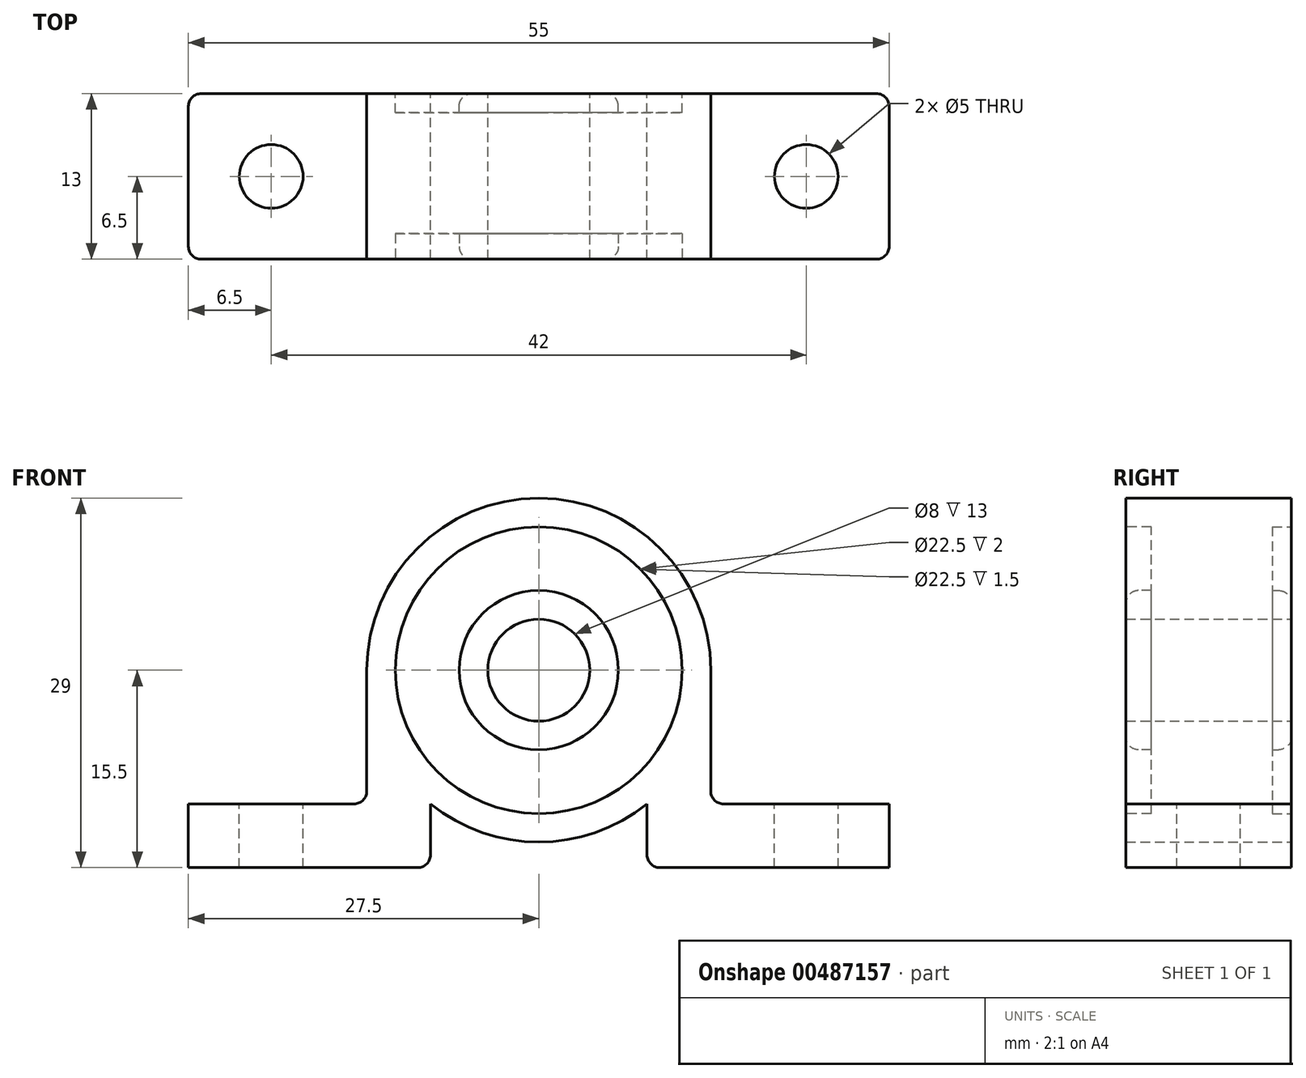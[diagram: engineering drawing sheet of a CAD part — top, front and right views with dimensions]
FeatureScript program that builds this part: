
annotation { "Feature Type Name" : "Feature", "Feature Type Description" : "" }
export const myFeature = defineFeature(function(context is Context, id is Id, definition is map)
    precondition{}
    {
        {
            var Q0;
            Q0=qCreatedBy(makeId("Front.planeOp"),FACE);
            var sketch = newSketch(context, id + "F0", { "sketchPlane" : qUnion([Q0])});
            skLineSegment(sketch, "E0.bottom", {"start": v(-27.5, 0) * mm, "end": v(-8.5, 0) * mm});
            skLineSegment(sketch, "E0.top", {"start": v(-27.5, 5) * mm, "end": v(-13.5, 5) * mm});
            skLineSegment(sketch, "E0.left", {"start": v(-27.5, 0) * mm, "end": v(-27.5, 5) * mm});
            skLineSegment(sketch, "E0.right", {"start": v(27.5, 0) * mm, "end": v(27.5, 5) * mm});
            skArc(sketch, "E1", {"start": v(-8.5, 5.01) * mm, "mid": v(0, 2) * mm, "end": v(8.5, 5.01) * mm});
            skCircle(sketch, "E2", {"center": v(0, 15.5) * mm, "radius": 4 * mm});
            skLineSegment(sketch, "E3", {"start": v(-13.5, 15.5) * mm, "end": v(-13.5, 5) * mm});
            skLineSegment(sketch, "E4", {"start": v(13.5, 15.5) * mm, "end": v(13.5, 5) * mm});
            skLineSegment(sketch, "E5", {"start": v(-8.5, 5.01) * mm, "end": v(-8.5, 0) * mm});
            skLineSegment(sketch, "E6", {"start": v(8.5, 5.01) * mm, "end": v(8.5, 0) * mm});
            skLineSegment(sketch, "E7.trimOffspring", {"start": v(8.5, 0) * mm, "end": v(27.5, 0) * mm});
            skLineSegment(sketch, "E8.trimOffspring", {"start": v(-8.5, 5) * mm, "end": v(-8.49, 5) * mm});
            skLineSegment(sketch, "E9.trimOffspring", {"start": v(8.49, 5) * mm, "end": v(8.5, 5) * mm});
            skArc(sketch, "E10.trimOffspring", {"start": v(13.5, 15.5) * mm, "mid": v(0, 29) * mm, "end": v(-13.5, 15.5) * mm});
            skLineSegment(sketch, "E11.trimOffspring", {"start": v(13.5, 5) * mm, "end": v(27.5, 5) * mm});
            skSolve(sketch);
        }
        {
            var Q0;
            Q0 = qSketchRegion(id + "F0", true);
            extrude(context, id + "F1", {"entities" : qUnion([Q0]), "depth" : 6.5 * mm, "hasSecondDirection" : true, "secondDirectionOppositeDirection" : true, "secondDirectionDepth" : 6.5 * mm});
        }
        {
            var Q0;
            Q0=makeQuery(id+"F1.opExtrude","SWEPT_FACE",FACE,{"disambiguationData":[OSD([sQuery(id+"F0.wireOp",EDGE,"E0.top")])]});
            var sketch = newSketch(context, id + "F2", { "sketchPlane" : qUnion([Q0])});
            skCircle(sketch, "E12", {"center": v(-21, 0) * mm, "radius": 2.5 * mm});
            skCircle(sketch, "E13", {"center": v(21, 0) * mm, "radius": 2.5 * mm});
            skSolve(sketch);
        }
        {
            var Q0;
            Q0 = qSketchRegion(id + "F2", true);
            extrude(context, id + "F3", {"entities" : qUnion([Q0]), "operationType" : NewBodyOperationType.REMOVE, "oppositeDirection" : true, "depth" : 25 * mm});
        }
        {
            var Q0;
            Q0=makeQuery(id+"F1.opExtrude","CAP_EDGE",EDGE,{"disambiguationData":[OSD([sQuery(id+"F0.wireOp",EDGE,"E0.left")])],"isStart":false});
            var Q1;
            Q1=makeQuery(id+"F1.opExtrude","CAP_EDGE",EDGE,{"disambiguationData":[OSD([sQuery(id+"F0.wireOp",EDGE,"E0.left")])],"isStart":true});
            var Q2;
            Q2=makeQuery(id+"F1.opExtrude","CAP_EDGE",EDGE,{"disambiguationData":[OSD([sQuery(id+"F0.wireOp",EDGE,"E0.right")])],"isStart":false});
            var Q3;
            Q3=makeQuery(id+"F1.opExtrude","CAP_EDGE",EDGE,{"disambiguationData":[OSD([sQuery(id+"F0.wireOp",EDGE,"E0.right")])],"isStart":true});
            var Q4;
            Q4=makeQuery(id+"F1.opExtrude","SWEPT_EDGE",EDGE,{"disambiguationData":[OSD([sQuery(id+"F0.wireOp",EDGE,"E4"),sQuery(id+"F0.wireOp",EDGE,"E11.trimOffspring")])]});
            var Q5;
            Q5=makeQuery(id+"F1.opExtrude","SWEPT_EDGE",EDGE,{"disambiguationData":[OSD([sQuery(id+"F0.wireOp",EDGE,"E6"),sQuery(id+"F0.wireOp",EDGE,"E7.trimOffspring")])]});
            var Q6;
            Q6=makeQuery(id+"F1.opExtrude","SWEPT_EDGE",EDGE,{"disambiguationData":[OSD([sQuery(id+"F0.wireOp",EDGE,"E0.bottom"),sQuery(id+"F0.wireOp",EDGE,"E5")])]});
            var Q7;
            Q7=makeQuery(id+"F1.opExtrude","SWEPT_EDGE",EDGE,{"disambiguationData":[OSD([sQuery(id+"F0.wireOp",EDGE,"E0.top"),sQuery(id+"F0.wireOp",EDGE,"E3")])]});
            fillet(context, id + "F4", {"entities" : qUnion([Q0, Q1, Q2, Q3, Q4, Q5, Q6, Q7]), "radius" : 1 * mm, "tangentPropagation" : true, "allowEdgeOverflow" : false});
        }
        {
            var Q0;
            Q0=makeQuery(id+"F1.opExtrude","CAP_FACE",FACE,{"disambiguationData":[OSD([sQuery(id+"F0.wireOp",EDGE,"E0.bottom"),sQuery(id+"F0.wireOp",EDGE,"E0.top"),sQuery(id+"F0.wireOp",EDGE,"E0.left"),sQuery(id+"F0.wireOp",EDGE,"E0.right"),sQuery(id+"F0.wireOp",EDGE,"E1"),sQuery(id+"F0.wireOp",EDGE,"E2"),sQuery(id+"F0.wireOp",EDGE,"E3"),sQuery(id+"F0.wireOp",EDGE,"E4"),sQuery(id+"F0.wireOp",EDGE,"E5"),sQuery(id+"F0.wireOp",EDGE,"E6"),sQuery(id+"F0.wireOp",EDGE,"E7.trimOffspring"),sQuery(id+"F0.wireOp",EDGE,"E8.trimOffspring"),sQuery(id+"F0.wireOp",EDGE,"E9.trimOffspring"),sQuery(id+"F0.wireOp",EDGE,"E10.trimOffspring"),sQuery(id+"F0.wireOp",EDGE,"E11.trimOffspring")])],"isStart":false});
            var sketch = newSketch(context, id + "F5", { "sketchPlane" : qUnion([Q0])});
            skCircle(sketch, "E14", {"center": v(0, 15.5) * mm, "radius": 11.25 * mm});
            skCircle(sketch, "E15", {"center": v(0, 15.5) * mm, "radius": 6.25 * mm});
            skSolve(sketch);
        }
        {
            var Q0;
            Q0 = qSketchRegion(id + "F5", true);
            extrude(context, id + "F6", {"entities" : qUnion([Q0]), "operationType" : NewBodyOperationType.REMOVE, "oppositeDirection" : true, "depth" : 2 * mm});
        }
        {
            var Q0;
            Q0=makeQuery(id+"F1.opExtrude","CAP_FACE",FACE,{"disambiguationData":[OSD([sQuery(id+"F0.wireOp",EDGE,"E0.bottom"),sQuery(id+"F0.wireOp",EDGE,"E0.top"),sQuery(id+"F0.wireOp",EDGE,"E0.left"),sQuery(id+"F0.wireOp",EDGE,"E0.right"),sQuery(id+"F0.wireOp",EDGE,"E1"),sQuery(id+"F0.wireOp",EDGE,"E2"),sQuery(id+"F0.wireOp",EDGE,"E3"),sQuery(id+"F0.wireOp",EDGE,"E4"),sQuery(id+"F0.wireOp",EDGE,"E5"),sQuery(id+"F0.wireOp",EDGE,"E6"),sQuery(id+"F0.wireOp",EDGE,"E7.trimOffspring"),sQuery(id+"F0.wireOp",EDGE,"E8.trimOffspring"),sQuery(id+"F0.wireOp",EDGE,"E9.trimOffspring"),sQuery(id+"F0.wireOp",EDGE,"E10.trimOffspring"),sQuery(id+"F0.wireOp",EDGE,"E11.trimOffspring")])],"isStart":true});
            var sketch = newSketch(context, id + "F7", { "sketchPlane" : qUnion([Q0])});
            skCircle(sketch, "E16", {"center": v(0, 15.5) * mm, "radius": 6.25 * mm});
            skCircle(sketch, "E17", {"center": v(0, 15.5) * mm, "radius": 11.25 * mm});
            skSolve(sketch);
        }
        {
            var Q0;
            Q0 = qSketchRegion(id + "F7", true);
            extrude(context, id + "F8", {"entities" : qUnion([Q0]), "operationType" : NewBodyOperationType.REMOVE, "oppositeDirection" : true, "depth" : 1.5 * mm});
        }
        {
            var Q0;
            Q0=makeQuery(id+"F8.boolean.opBoolean","COPY",EDGE,{"derivedFrom":makeQuery(id+"F8.opExtrude","CAP_EDGE",EDGE,{"disambiguationData":[OSD([sQuery(id+"F7.wireOp",EDGE,"E17")])],"isStart":true})});
            var Q1;
            Q1=makeQuery(id+"F8.boolean.opBoolean","COPY",EDGE,{"derivedFrom":makeQuery(id+"F8.opExtrude","CAP_EDGE",EDGE,{"disambiguationData":[OSD([sQuery(id+"F7.wireOp",EDGE,"E16")])],"isStart":true})});
            var Q2;
            Q2=makeQuery(id+"F6.boolean.opBoolean","COPY",EDGE,{"derivedFrom":makeQuery(id+"F6.opExtrude","CAP_EDGE",EDGE,{"disambiguationData":[OSD([sQuery(id+"F5.wireOp",EDGE,"E14")])],"isStart":true})});
            var Q3;
            Q3=makeQuery(id+"F6.boolean.opBoolean","COPY",EDGE,{"derivedFrom":makeQuery(id+"F6.opExtrude","CAP_EDGE",EDGE,{"disambiguationData":[OSD([sQuery(id+"F5.wireOp",EDGE,"E15")])],"isStart":true})});
            fillet(context, id + "F9", {"entities" : qUnion([Q0, Q1, Q2, Q3]), "radius" : 1 * mm, "tangentPropagation" : true, "allowEdgeOverflow" : false});
        }
    });
